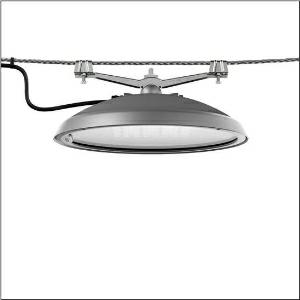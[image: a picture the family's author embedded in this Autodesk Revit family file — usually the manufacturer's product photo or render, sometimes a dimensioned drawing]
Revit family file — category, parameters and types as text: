
# Revit family: dl_50_iq_mini___p1_0s_5xa248u31f08fe_8e62
name_source: partatom
category: Lighting Fixtures
units: mm (PartAtom-declared; Revit-internal decimal feet)

## family parameters
Cut with Voids When Loaded = No
Host = Face
Light Source = No
Part Type = Normal
Room Calculation Point = No
Round Connector Dimension = Use Diameter
Shared = No

## types (1)
- --- (1 x LED, 2610 lm, 16.3 W, 3000K)
    Apparent Load = 16 VA
    CIE Flux Codes = 23 54 93 100 100
    Color Rendering = 70
    Color Temperature = 3000K
    Default Elevation = 1800 mm
    Description = DL 50 iQ mini, catenary luminaire, primary light control with lens, of PMMA, primary optical cover: cover, of toughened safety glass, transparent, light distribution: P1.0s, light emission: direct distribution, primary light characteristic: symmetric, installation type: suspended mounting, LED, High Power LED, rated luminous flux: 2.610lm, luminous efficacy: 160lm/W, light colour: 730, colour temperature: 3000K, control gear: iQ Street-Remote, control: optimised constant luminous flux control (CLO 2.0), Desk-Remote (wireless, voltage-free reading and setting of iQ features in the workshop via application-optimized NFC function/RFID function), Light-Fading, Smart-Wire, Night-Set, Lumen-Switch, Temp-Guard, Auto-Match, Street-Remote, mains connection: 230..240V, AC, 50/60Hz, start of lifetime: 16W, end of service life: 17W, reduction: 8W, luminaire housing, of diecast aluminium, powder-coated, SITECO metallic grey (DB 702S), diameter: 500mm, height: 115mm, mounting height: 4..12m, protection rating (complete): IP66, insulation class (complete): insulation class II (safety insulation), certification: CE, ENEC, ENEC+, VDE, impact resistance: IK08, permissible operating ambient temperature for outdoor applications: -25..+40°C, standard-compliant lighting for roads and squares, packaging unit: 1 piece

Light Distribution: P1.0s
    Height = 124 mm  [stored 0.406824 ft]
    Lamp = 1 x LED
    Lamp Light Flux = 2610 lm
    Lamp Power = 16.3 W
    Lamp count = 1
    Length = 500 mm
    Luminous efficacy = 160 lm/W
    Manufacturer = Siteco
    ModVariant = No
    Model = 5XA248U31F08FE
    Number of Poles = 1
    OnlyDefault = Yes
    Power Factor = 1
    Product Name = DL 50 iQ mini | P1.0s
    Product group = catenary luminaire
    ProductGroupID = 6300
    Protection Class = Protection class II
    Protection Degree = IP 66
    RLX_Detail_Level = 1
    RLX_Emergency_Light_Flux = 0 lm
    RLX_Emergency_Type = 0
    RLX_Emergency_Type_DB = No
    RlxData = <blob elided: 123481 chars, md5=54e66724>
    Socket = socket
    Standby Power = 0 W
    System Light Flux = 2610 lm
    System Power = 16 W
    Type Comments = factory setting: luminous flux: 100 % | dim-lin: 254 | 333 mA
    Type Image = l_1242791.jpg
    URL = http://relux.com
    VarID = @adj_137289
    Voltage = 0 V
    Weight = 0.00 kg
    Width = 0 mm  [stored 0 ft]

note: [stored X ft] marks values corroborated as IEEE doubles in the binary element streams (Revit-internal decimal feet)

## geometry (parser evidence)
native form markers: Blend x4, Sweep x12
no freeform markers — native parametric forms only
